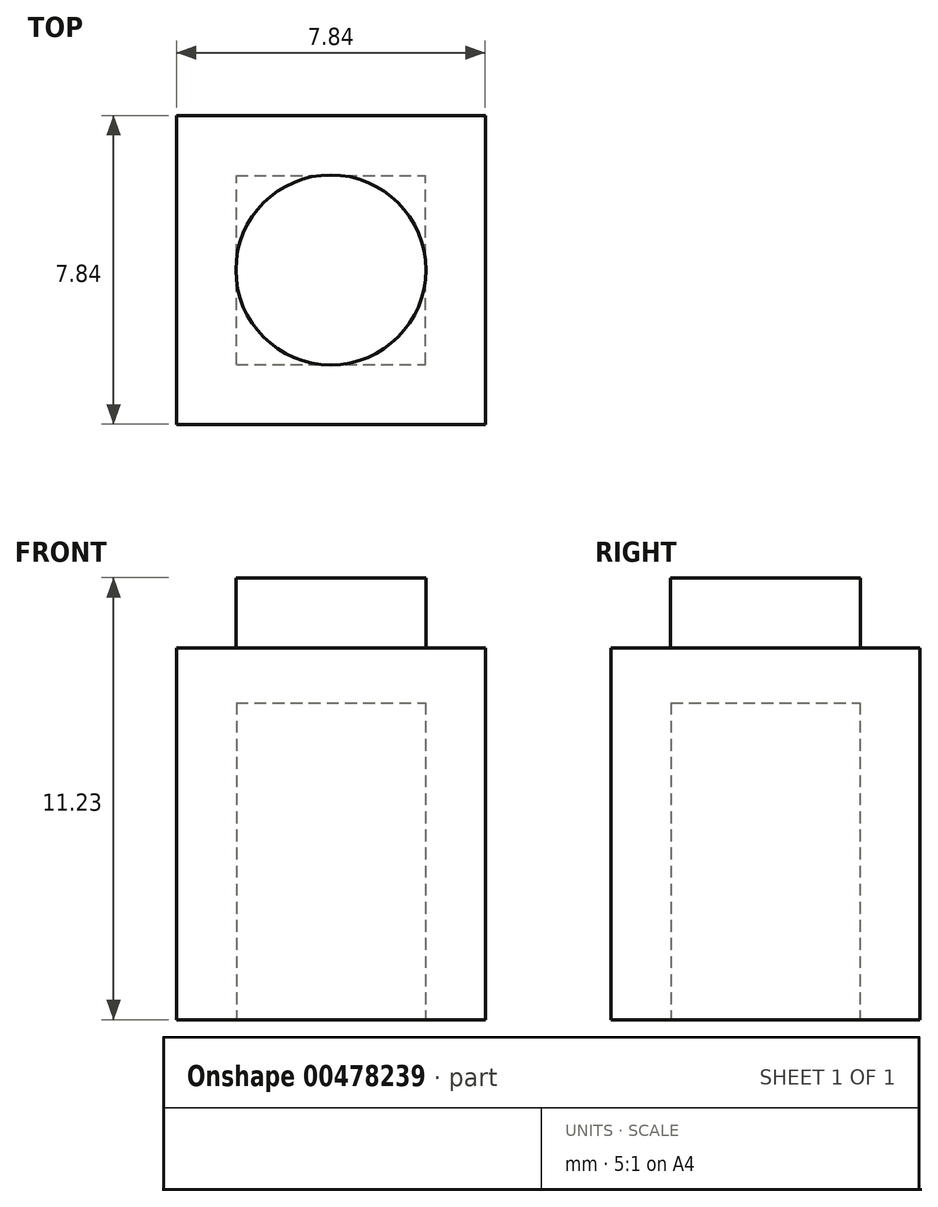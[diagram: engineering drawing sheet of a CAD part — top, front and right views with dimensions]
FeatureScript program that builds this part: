
annotation { "Feature Type Name" : "Feature", "Feature Type Description" : "" }
export const myFeature = defineFeature(function(context is Context, id is Id, definition is map)
    precondition{}
    {
        {
            var Q0;
            Q0=qCreatedBy(makeId("Top.planeOp"),FACE);
            var sketch = newSketch(context, id + "F0", { "sketchPlane" : qUnion([Q0])});
            skLineSegment(sketch, "E0.bottom", {"start": v(-3.92, 3.92) * mm, "end": v(3.92, 3.92) * mm});
            skLineSegment(sketch, "E0.top", {"start": v(-3.92, -3.92) * mm, "end": v(3.92, -3.92) * mm});
            skLineSegment(sketch, "E0.left", {"start": v(-3.92, 3.92) * mm, "end": v(-3.92, -3.92) * mm});
            skLineSegment(sketch, "E0.right", {"start": v(3.92, 3.92) * mm, "end": v(3.92, -3.92) * mm});
            skPoint(sketch, "E0.middle", {"position": v(0, 0) * mm});
            skSolve(sketch);
        }
        {
            var Q0;
            Q0=makeQuery(id+"F0.imprint","IMPRINT",FACE,{"disambiguationData":[TD([[makeQuery(id+"F0.imprint","IMPRINT",EDGE,{"derivedFrom":sQuery(id+"F0.wireOp",EDGE,"E0.bottom")}),-1.0]])]});
            extrude(context, id + "F1", {"entities" : qUnion([Q0]), "depth" : 9.45 * mm});
        }
        {
            var Q0;
            Q0=makeQuery(id+"F1.opExtrude","CAP_FACE",FACE,{"disambiguationData":[OSD([sQuery(id+"F0.wireOp",EDGE,"E0.bottom"),sQuery(id+"F0.wireOp",EDGE,"E0.top"),sQuery(id+"F0.wireOp",EDGE,"E0.left"),sQuery(id+"F0.wireOp",EDGE,"E0.right")])],"isStart":false});
            var sketch = newSketch(context, id + "F2", { "sketchPlane" : qUnion([Q0])});
            skCircle(sketch, "E1", {"center": v(0, 0) * mm, "radius": 2.41 * mm});
            skSolve(sketch);
        }
        {
            var Q0;
            Q0=makeQuery(id+"F2.imprint","IMPRINT",FACE,{"disambiguationData":[TD([[makeQuery(id+"F2.imprint","IMPRINT",EDGE,{"derivedFrom":sQuery(id+"F2.wireOp",EDGE,"E1")}),1.0]])]});
            extrude(context, id + "F3", {"entities" : qUnion([Q0]), "operationType" : NewBodyOperationType.ADD, "depth" : 1.78 * mm});
        }
        {
            var Q0;
            Q0=makeQuery(id+"F1.opExtrude","CAP_FACE",FACE,{"disambiguationData":[OSD([sQuery(id+"F0.wireOp",EDGE,"E0.bottom"),sQuery(id+"F0.wireOp",EDGE,"E0.top"),sQuery(id+"F0.wireOp",EDGE,"E0.left"),sQuery(id+"F0.wireOp",EDGE,"E0.right")])],"isStart":true});
            var sketch = newSketch(context, id + "F4", { "sketchPlane" : qUnion([Q0])});
            skLineSegment(sketch, "E2.bottom", {"start": v(-2.4, 2.4) * mm, "end": v(2.4, 2.4) * mm});
            skLineSegment(sketch, "E2.top", {"start": v(-2.4, -2.4) * mm, "end": v(2.4, -2.4) * mm});
            skLineSegment(sketch, "E2.left", {"start": v(-2.4, 2.4) * mm, "end": v(-2.4, -2.4) * mm});
            skLineSegment(sketch, "E2.right", {"start": v(2.4, 2.4) * mm, "end": v(2.4, -2.4) * mm});
            skPoint(sketch, "E2.middle", {"position": v(0, 0) * mm});
            skSolve(sketch);
        }
        {
            var Q0;
            Q0=makeQuery(id+"F4.imprint","IMPRINT",FACE,{"disambiguationData":[TD([[makeQuery(id+"F4.imprint","IMPRINT",EDGE,{"derivedFrom":sQuery(id+"F4.wireOp",EDGE,"E2.bottom")}),-1.0]])]});
            extrude(context, id + "F5", {"entities" : qUnion([Q0]), "operationType" : NewBodyOperationType.REMOVE, "depth" : -8.05 * mm});
        }
    });
